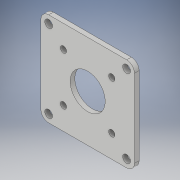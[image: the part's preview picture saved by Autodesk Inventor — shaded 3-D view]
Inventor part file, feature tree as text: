
AUTODESK INVENTOR PART (.ipt)
format: ipt  version: 2019.3 (Build 233278000, 278)  size: 148,480 bytes
history: native  units: mm
features: extrude x1, fillet x1, sketch x1
ambient origin geometry x8: Origin, YZ Plane, XZ Plane, XY Plane, X Axis, Y Axis, Z Axis, Center Point
bodies: Solid1 (feature_tree)
feature tree (3):
  extrude  "Extrusion1"  Depth=5.0mm
  fillet  "Fillet1"  Radius=4.0mm
  sketch  "Sketch1"  dims[d0=4.0mm d1=4.0mm d2=4.0mm d3=4.0mm d4=22.5mm d5=31.0mm d6=31.0mm d7=31.0mm d8=31.0mm d9=15.5mm d10=15.5mm d11=15.5mm d12=15.5mm d13=60.0mm d14=60.0mm d15=30.0mm d16=30.0mm d17=5.0mm d18=5.0mm d19=5.0mm d20=5.0mm d21=50.0mm d22=50.0mm d23=50.0mm d24=50.0mm d25=5.0mm d26=5.0mm d27=5.0mm d28=5.0mm d29=3.0mm d30=0.0mm d31=5.0mm]
